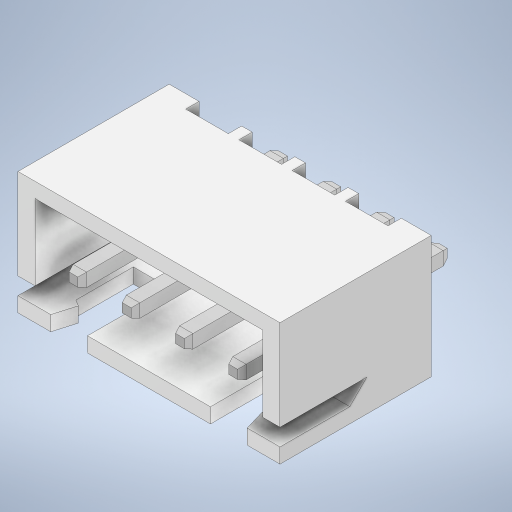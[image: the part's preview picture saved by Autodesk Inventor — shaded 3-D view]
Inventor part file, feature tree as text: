
AUTODESK INVENTOR PART (.ipt)
format: ipt  version: 2023 (Build 270158000, 158)  size: 486,912 bytes
history: native  units: mm
features: extrude x2, sketch x2, imported_body x1
ambient origin geometry x8: Origin, YZ Plane, XZ Plane, XY Plane, X Axis, Y Axis, Z Axis, Center Point
bodies: Solid1 (feature_tree)
feature tree (5):
  extrude  "Extrusion1"  TaperAngle=0.0deg  [1 undecoded]
  extrude  "Extrusion2"  TaperAngle=0.0deg  [1 undecoded]
  sketch  "Sketch1"  dims[d0=12.5mm d1=0.0mm]
  sketch  "Sketch2"  dims[d2=-0.103mm d3=0.0mm d4=0.0mm d5=17.5mm d6=5.0mm d7=0.0mm d8=0.0mm]
  imported_body  "Base1"
note: 2 required parameter values undecoded (feature->parameter linkage not recoverable at this tier; creation-order binding heuristic only, values carry confidence <= 0.55)
